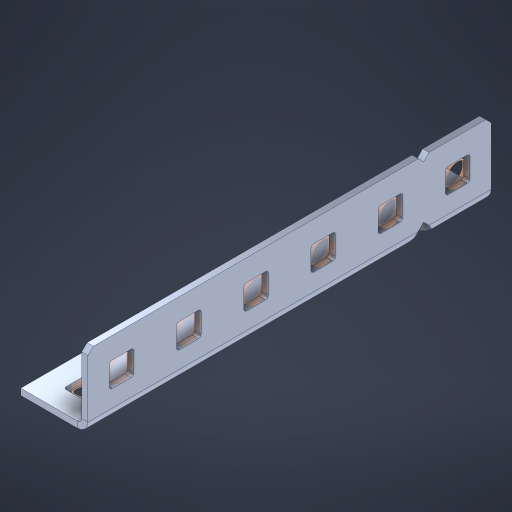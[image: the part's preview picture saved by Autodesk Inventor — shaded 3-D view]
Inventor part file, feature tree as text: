
AUTODESK INVENTOR PART (.ipt)
format: ipt  version: 2023 (Build 270158000, 158)  size: 476,672 bytes
history: native  units: in
note: dims shown in document units (in); Inventor stores cm internally (conversion verified against a paired STEP export)
features: other x17, extrude x11, sheet_metal_op x10, sketch x8, mirror x1, pattern_linear x1, chamfer x1
ambient origin geometry x8: Origin, YZ Plane, XZ Plane, XY Plane, X Axis, Y Axis, Z Axis, Center Point
bodies: Solid1 (feature_tree), Body (feature_tree)
feature tree (49):
  other  "Flange Pattern Plane"
  sheet_metal_op  "Flange Pattern"
  sheet_metal_op  "Body Pattern"
  other  "Arc Length"
  mirror  "Notch Mirror"
  pattern_linear  "Notch Pattern"  Spacing1=0.1875in  [1 undecoded]
  chamfer  "End Chamfer"
  extrude  "Half Cut"  Depth=0.0469in
  sketch  "Sketch1"  dims[d0=2.5in]
  other  "Plate1"
  sketch  "Sketch2"  dims[d1=3.0in]
  other  "Plate2"
  sheet_metal_op  "Bend1"
  sheet_metal_op  "Corner1"
  sketch  "Sketch3"  dims[d2=0.0469in]
  other  "Flange Pattern Sketch"
  sketch  "Sketch7"  dims[d3=0.0469in]
  other  "Srf1"
  other  "Srf2"
  sketch  "Sketch8"  dims[d4=0.0234in]
  sketch  "Sketch9"  dims[d5=0.0938in]
  other  "Srf91"
  sheet_metal_op  "Body Pattern Sketch"
  other  "Srf92"
  sketch  "Sketch13"  dims[d6=0.0469in]
  sketch  "Sketch14"  dims[d7=0.5in d8=90.0deg d9=0.0312in d10=0.1875in d11=0.0469in d12=0.0469in d16=0.182in d17=0.02in d18=0.0469in d19=0.0in d20=0.25in d21=0.25in d46=0.172in d47=1.0in d48=0.0in d49=0.182in d50=0.02in d51=0.25in d52=0.25in d53=0.0469in d54=0.0in d55=0.172in d56=1.0in d57=0.0in d60=2.3622in d62=0.5in d63=0.3937in d65=0.5in d85=0.1227in d86=0.1659in d88=0.04in d89=0.0469in d90=0.0in d91=0.04in d92=0.0491in d95=2.5in d96=0.04in d97=0.25in d98=45.0deg d101=0.0in d102=2.497in d131=0.5in d132=2.3622in d134=0.5in d139=0.5in]
  other  "Srf856"
  other  "Srf1310"
  other  "Srf1311"
  other  "Srf1312"
  other  "Srf1376"
  other  "Srf1377"
  other  "Srf1728"
  other  "Srf1755"
  sheet_metal_op  "Flange Stamp"
  sheet_metal_op  "Flange Circle"
  sheet_metal_op  "Body Stamp"
  sheet_metal_op  "Body Circle"
  sheet_metal_op  "Notch"
  extrude  "ExtrusionSrf2"  Depth=0.0469in
  extrude  "ExtrusionSrf92"  Depth=0.5in
  extrude  "ExtrusionSrf856"  Depth=0.02in
  extrude  "ExtrusionSrf1310"  Depth=0.0469in
  extrude  "ExtrusionSrf1311"  TaperAngle=0.0deg  [1 undecoded]
  extrude  "ExtrusionSrf1312"  Depth=0.5in
  extrude  "ExtrusionSrf1376"  Depth=0.5in
  extrude  "ExtrusionSrf1377"  Depth=0.5in
  extrude  "ExtrusionSrf1728"  Depth=0.5in TaperAngle=0.0deg
  extrude  "ExtrusionSrf1755"  Depth=0.5in
note: 2 required parameter values undecoded (feature->parameter linkage not recoverable at this tier; creation-order binding heuristic only, values carry confidence <= 0.55)
